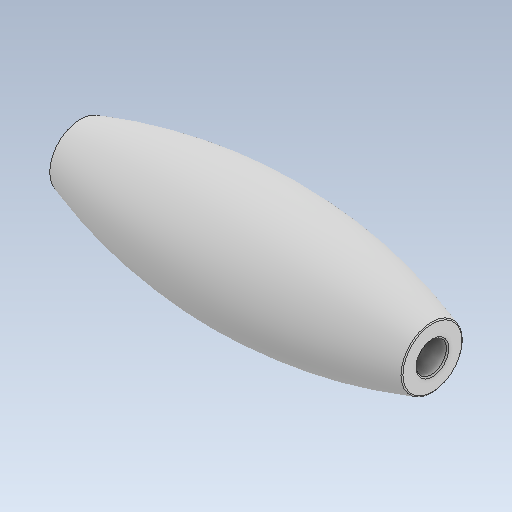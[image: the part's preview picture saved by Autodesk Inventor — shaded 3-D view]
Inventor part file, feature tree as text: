
AUTODESK INVENTOR PART (.ipt)
format: ipt  version: 2020.2 (Build 242310000, 310)  size: 119,296 bytes
history: native  units: in
note: dims shown in document units (in); Inventor stores cm internally (conversion verified against a paired STEP export)
features: fillet x1
ambient origin geometry x8: Origin, YZ Plane, XZ Plane, XY Plane, X Axis, Y Axis, Z Axis, Center Point
bodies: Solid1 (feature_tree)
feature tree (1):
  fillet  "Fillet1"  [1 undecoded]
note: 1 required parameter value undecoded (feature->parameter linkage not recoverable at this tier; creation-order binding heuristic only, values carry confidence <= 0.55)
